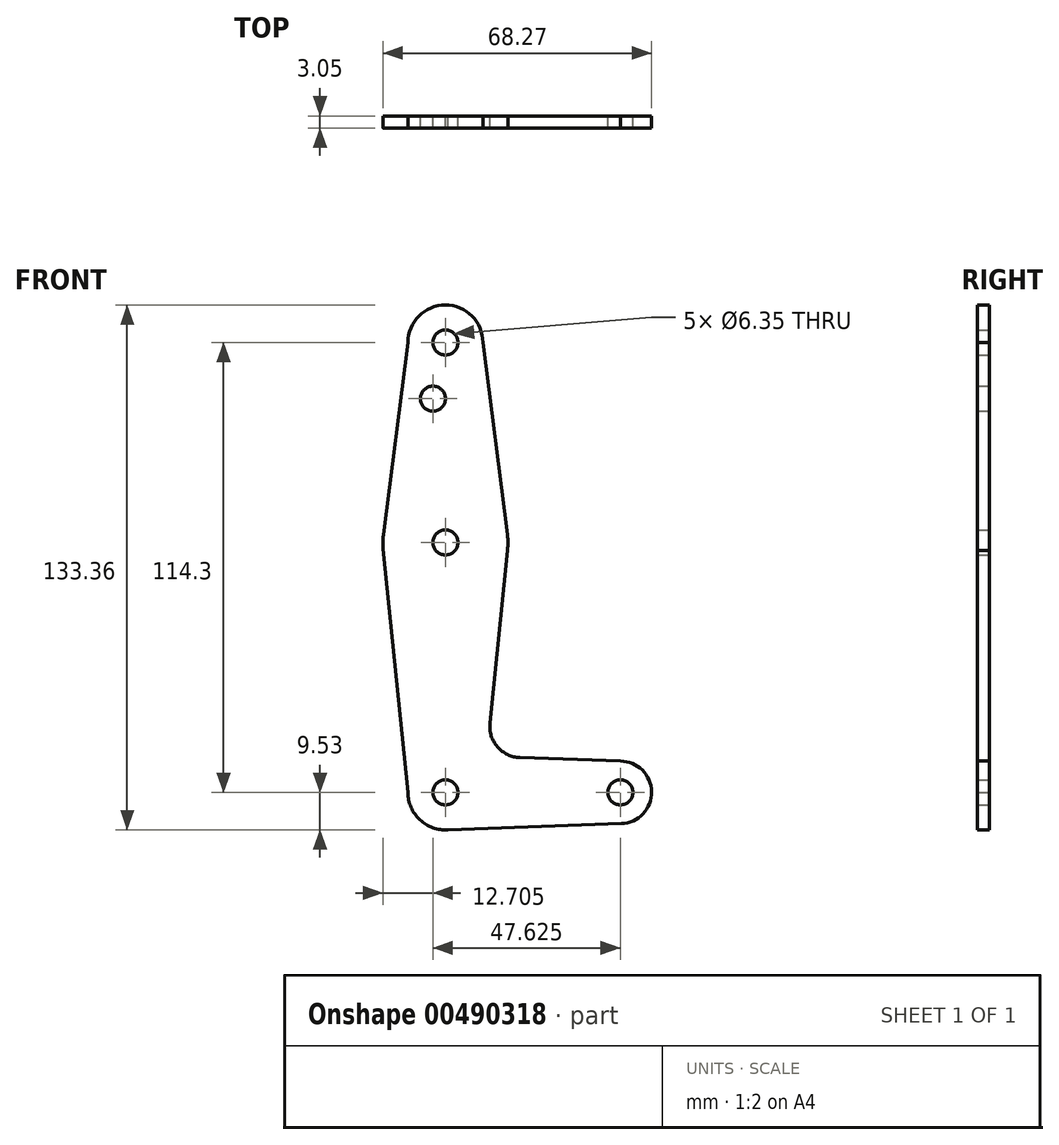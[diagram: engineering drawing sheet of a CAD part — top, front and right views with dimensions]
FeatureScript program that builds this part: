
annotation { "Feature Type Name" : "Feature", "Feature Type Description" : "" }
export const myFeature = defineFeature(function(context is Context, id is Id, definition is map)
    precondition{}
    {
        {
            var Q0;
            Q0=qCreatedBy(makeId("Front.planeOp"),FACE);
            var sketch = newSketch(context, id + "F0", { "sketchPlane" : qUnion([Q0])});
            skLineSegment(sketch, "E0", {"start": v(0, 0) * mm, "end": v(0, 114.3) * mm, "construction": true});
            skLineSegment(sketch, "E1", {"start": v(0, 0) * mm, "end": v(44.45, 0) * mm, "construction": true});
            skCircle(sketch, "E2", {"center": v(0, 114.3) * mm, "radius": 9.53 * mm});
            skCircle(sketch, "E3", {"center": v(0, 63.5) * mm, "radius": 15.88 * mm});
            skCircle(sketch, "E4", {"center": v(0, 0) * mm, "radius": 9.53 * mm});
            skCircle(sketch, "E5", {"center": v(44.45, 0) * mm, "radius": 7.94 * mm});
            skLineSegment(sketch, "E6", {"start": v(9.53, 114.3) * mm, "end": v(15.75, 65.5) * mm});
            skLineSegment(sketch, "E7", {"start": v(-9.53, 114.3) * mm, "end": v(-15.75, 65.5) * mm});
            skLineSegment(sketch, "E8", {"start": v(-9.53, 0) * mm, "end": v(-15.8, 61.9) * mm});
            skLineSegment(sketch, "E9", {"start": v(11.3, 17.6) * mm, "end": v(15.75, 61.5) * mm});
            skLineSegment(sketch, "E10", {"start": v(18.93, 8.85) * mm, "end": v(44.45, 7.94) * mm});
            skLineSegment(sketch, "E11", {"start": v(0, -9.53) * mm, "end": v(44.73, -7.93) * mm});
            skCircle(sketch, "E12", {"center": v(-3.18, 100.03) * mm, "radius": 3.18 * mm});
            skCircle(sketch, "E13", {"center": v(0, 114.3) * mm, "radius": 3.18 * mm});
            skCircle(sketch, "E14", {"center": v(0, 63.5) * mm, "radius": 3.18 * mm});
            skCircle(sketch, "E15", {"center": v(0, 0) * mm, "radius": 3.18 * mm});
            skCircle(sketch, "E16", {"center": v(44.45, 0) * mm, "radius": 3.18 * mm});
            skArc(sketch, "E17.filletArc", {"start": v(11.3, 17.6) * mm, "mid": v(13.22, 11.57) * mm, "end": v(18.93, 8.85) * mm});
            skSolve(sketch);
        }
        {
            var Q0;
            Q0 = qSketchRegion(id + "F0", true);
            extrude(context, id + "F1", {"entities" : qUnion([Q0]), "depth" : 3.05 * mm});
        }
    });
